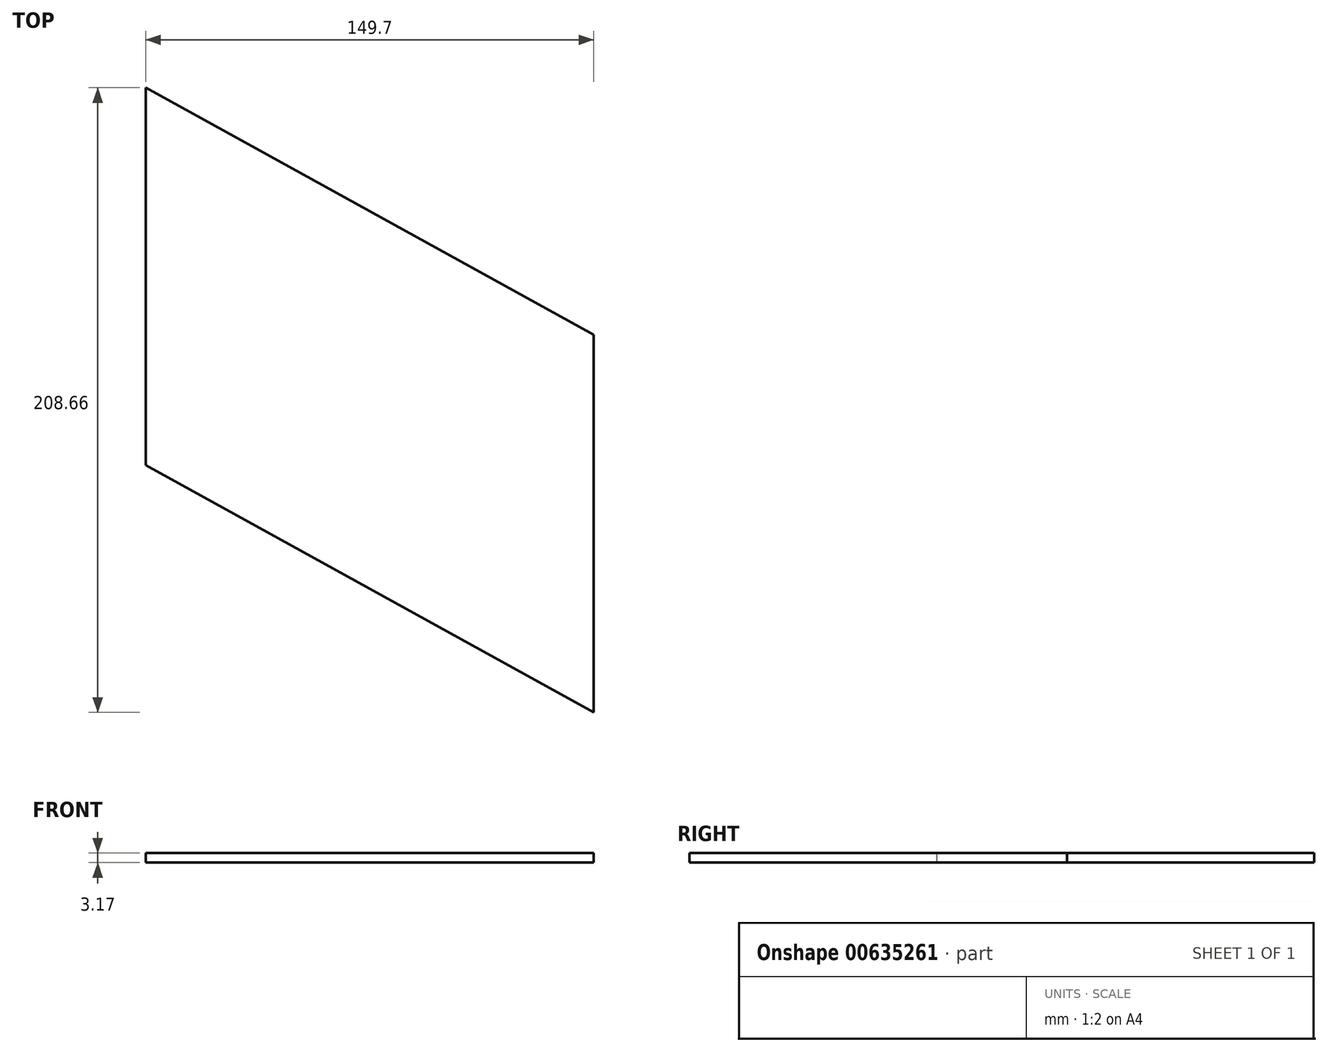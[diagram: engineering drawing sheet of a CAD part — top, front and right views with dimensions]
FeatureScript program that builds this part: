
annotation { "Feature Type Name" : "Feature", "Feature Type Description" : "" }
export const myFeature = defineFeature(function(context is Context, id is Id, definition is map)
    precondition{}
    {
        {
            var Q0;
            Q0=qCreatedBy(makeId("Top.planeOp"),FACE);
            var sketch = newSketch(context, id + "F0", { "sketchPlane" : qUnion([Q0])});
            skLineSegment(sketch, "E0.left", {"start": v(0, 0) * mm, "end": v(0, 126.11) * mm});
            skLineSegment(sketch, "E1", {"start": v(0, 0) * mm, "end": v(-149.7, 82.55) * mm});
            skLineSegment(sketch, "E2", {"start": v(-149.7, 82.55) * mm, "end": v(-149.7, 208.66) * mm});
            skLineSegment(sketch, "E3", {"start": v(-149.7, 208.66) * mm, "end": v(0, 126.11) * mm});
            skSolve(sketch);
        }
        {
            var Q0;
            Q0 = qSketchRegion(id + "F0", true);
            extrude(context, id + "F1", {"entities" : qUnion([Q0]), "depth" : 3.17 * mm, "offsetDistance" : 25.4 * mm});
        }
    });
